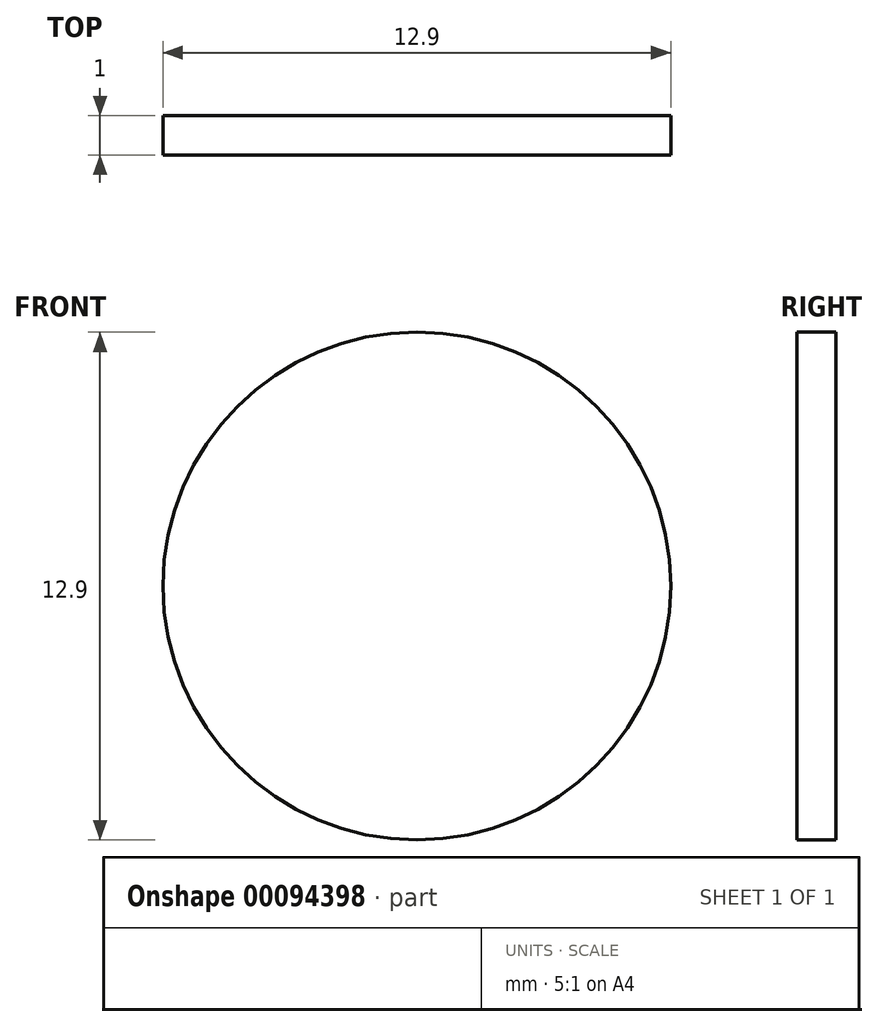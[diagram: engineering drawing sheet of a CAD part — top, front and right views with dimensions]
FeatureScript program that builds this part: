
annotation { "Feature Type Name" : "Feature", "Feature Type Description" : "" }
export const myFeature = defineFeature(function(context is Context, id is Id, definition is map)
    precondition{}
    {
        {
            var Q0;
            Q0=qCreatedBy(makeId("Front.planeOp"),FACE);
            var sketch = newSketch(context, id + "F0", { "sketchPlane" : qUnion([Q0])});
            skCircle(sketch, "E0", {"center": v(0, 0) * mm, "radius": 6.45 * mm});
            skSolve(sketch);
        }
        {
            var Q0;
            Q0 = qSketchRegion(id + "F0", true);
            var Q1;
            Q1=makeQuery(id+"F0.imprint","IMPRINT",FACE,{"disambiguationData":[TD([[makeQuery(id+"F0.imprint","IMPRINT",EDGE,{"derivedFrom":sQuery(id+"F0.wireOp",EDGE,"E0")}),1.0]])]});
            extrude(context, id + "F1", {"entities" : qUnion([Q0, Q1]), "depth" : 1 * mm});
        }
    });
